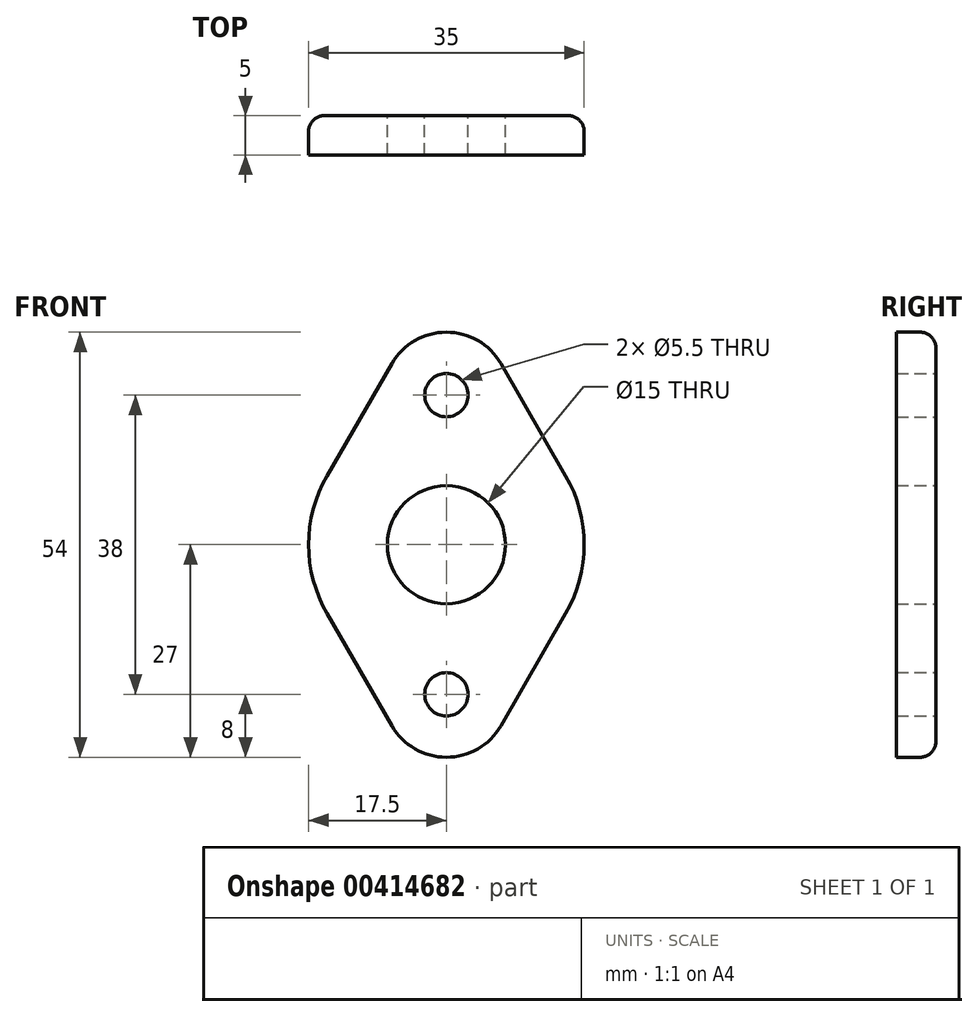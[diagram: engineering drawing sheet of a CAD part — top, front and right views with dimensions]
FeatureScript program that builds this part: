
annotation { "Feature Type Name" : "Feature", "Feature Type Description" : "" }
export const myFeature = defineFeature(function(context is Context, id is Id, definition is map)
    precondition{}
    {
        {
            var Q0;
            Q0=qCreatedBy(makeId("Front.planeOp"),FACE);
            var sketch = newSketch(context, id + "F0", { "sketchPlane" : qUnion([Q0])});
            skLineSegment(sketch, "E0", {"start": v(-25.9, 0) * mm, "end": v(25.62, 0) * mm, "construction": true});
            skLineSegment(sketch, "E1", {"start": v(0, -30.3) * mm, "end": v(0, 33.72) * mm, "construction": true});
            skArc(sketch, "E2", {"start": v(-15.16, 8.75) * mm, "mid": v(-17.5, 0) * mm, "end": v(-15.16, -8.75) * mm});
            skCircle(sketch, "E3", {"center": v(0, 0) * mm, "radius": 7.5 * mm});
            skLineSegment(sketch, "E4", {"start": v(6.93, 23) * mm, "end": v(15.16, 8.75) * mm});
            skLineSegment(sketch, "E5", {"start": v(-6.93, 23) * mm, "end": v(-15.16, 8.75) * mm});
            skArc(sketch, "E6.trimOffspring", {"start": v(6.93, 23) * mm, "mid": v(0, 27) * mm, "end": v(-6.93, 23) * mm});
            skCircle(sketch, "E7", {"center": v(0, 19) * mm, "radius": 2.75 * mm});
            skLineSegment(sketch, "E8.MirrorCS", {"start": v(6.93, -23) * mm, "end": v(15.16, -8.75) * mm});
            skArc(sketch, "E9.MirrorCS", {"start": v(6.93, -23) * mm, "mid": v(0, -27) * mm, "end": v(-6.93, -23) * mm});
            skCircle(sketch, "E10.MirrorC", {"center": v(0, -19) * mm, "radius": 2.75 * mm});
            skLineSegment(sketch, "E11.MirrorCS", {"start": v(-6.93, -23) * mm, "end": v(-15.16, -8.75) * mm});
            skArc(sketch, "E12.trimOffspring", {"start": v(15.16, -8.75) * mm, "mid": v(17.5, 0) * mm, "end": v(15.16, 8.75) * mm});
            skSolve(sketch);
        }
        {
            var Q0;
            Q0 = qSketchRegion(id + "F0", true);
            extrude(context, id + "F1", {"entities" : qUnion([Q0]), "depth" : 5 * mm});
        }
        {
            var Q0;
            Q0=makeQuery(id+"F1.opExtrude","CAP_EDGE",EDGE,{"disambiguationData":[OSD([sQuery(id+"F0.wireOp",EDGE,"E4")])],"isStart":true});
            fillet(context, id + "F2", {"entities" : qUnion([Q0]), "radius" : 2 * mm, "tangentPropagation" : true, "allowEdgeOverflow" : false});
        }
    });
